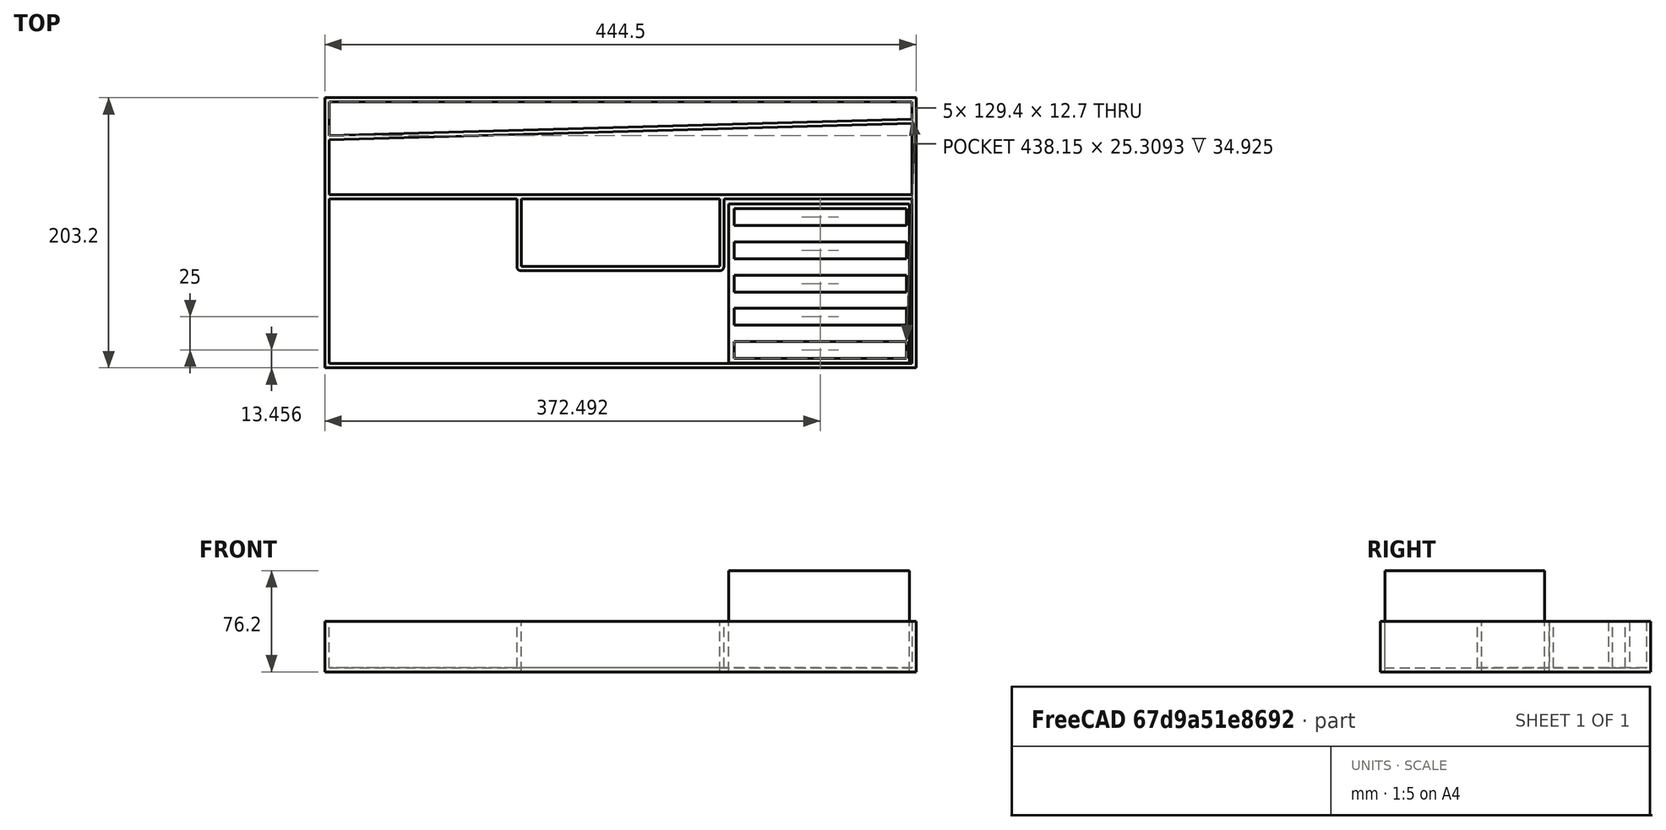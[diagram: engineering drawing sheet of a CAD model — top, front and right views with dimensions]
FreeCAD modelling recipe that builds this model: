
FCSTD DOCUMENT  (FreeCAD 0.19R24291 (Git))
Label: Tray
License: All rights reserved
LicenseURL: http://en.wikipedia.org/wiki/All_rights_reserved
objects: TechDraw::DrawViewDimension×15, Sketcher::SketchObject×5, PartDesign::Pad×4, TechDraw::DrawProjGroupItem×3, PartDesign::Body×2, App::Part×2, TechDraw::DrawSVGTemplate×2, TechDraw::DrawProjGroup×2, TechDraw::DrawPage×2, Spreadsheet::Sheet×1, PartDesign::Thickness×1, PartDesign::Pocket×1, PartDesign::LinearPattern×1
note: 20 computed .brp shape members not serialized (recipe doc carries the construction recipe); baked Part::Feature solids carry a one-line shape summary decoded from their .brp

FEATURE [Sketcher::SketchObject] Sketch
  FullyConstrained = true
  MapMode = 5
  Support = -> [XY_Plane001]
  expr: Constraints[21] = <<SpreadsheetTray>>.HandelPocket_x
  expr: Constraints[20] = <<SpreadsheetTray>>.HandelPocket_y
  expr: Constraints[10] = <<SpreadsheetTray>>.Width_y
  expr: Constraints[9] = <<SpreadsheetTray>>.Length_x
  sketch-geometry (8):
    g0: LineSegment StartX=-222.25 StartY=101.6 StartZ=0 EndX=222.25 EndY=101.6 EndZ=0
    g1: LineSegment StartX=222.25 StartY=101.6 StartZ=0 EndX=222.25 EndY=-101.6 EndZ=0
    g2: LineSegment StartX=222.25 StartY=-101.6 StartZ=0 EndX=-222.25 EndY=-101.6 EndZ=0
    g3: LineSegment StartX=-222.25 StartY=-101.6 StartZ=0 EndX=-222.25 EndY=101.6 EndZ=0
    g4: LineSegment StartX=-74.6125 StartY=25.4 StartZ=0 EndX=74.6125 EndY=25.4 EndZ=0
    g5: LineSegment StartX=74.6125 StartY=25.4 StartZ=0 EndX=74.6125 EndY=-25.4 EndZ=0
    g6: LineSegment StartX=74.6125 StartY=-25.4 StartZ=0 EndX=-74.6125 EndY=-25.4 EndZ=0
    g7: LineSegment StartX=-74.6125 StartY=-25.4 StartZ=0 EndX=-74.6125 EndY=25.4 EndZ=0
  constraints (22):
    c: Coincident(g0,g1)
    c: Coincident(g1,g2)
    c: Coincident(g2,g3)
    c: Coincident(g3,g0)
    c: Horizontal(g0)
    c: Horizontal(g2)
    c: Vertical(g1)
    c: Vertical(g3)
    c: Symmetric(g0,g1,g-1)
    c: DistanceX(g0,g0) = 444.5
    c: DistanceY(g2,g0) = 203.2
    c: Coincident(g4,g5)
    c: Coincident(g5,g6)
    c: Coincident(g6,g7)
    c: Coincident(g7,g4)
    c: Horizontal(g4)
    c: Horizontal(g6)
    c: Vertical(g5)
    c: Vertical(g7)
    c: Symmetric(g4,g5,g-1)
    c: DistanceY(g5,g4) = 50.8
    c: DistanceX(g6,g5) = 149.225
FEATURE [Spreadsheet::Sheet] Spreadsheet  label="SpreadsheetTray"
  cells = A2=Tray; A4=Length_x; B4(Length_x)==17.5in; C4=HalfLength; D4(HalfLength)==B4 / 2; A5=Width_y; B5(Width_y)==8in; C5=HalfWidth; D5(HalfWidth)==B5 / 2; A6=Height_z; B6(Height_z)==1.5in; A8=Thickness; B8(Thickness)==0.125"; A10=HandelPocket_x; B10(HandelPocket_x)==5.875"; A11=HandelPocket_y; B11(HandelPocket_y)==2"
FEATURE [PartDesign::Pad] Pad  label="PadHeight_z"
  Direction = (1,1,1)
  Length = 38.1
  Length2 = 99.9998
  Profile = -> Sketch
  Type = 0
  expr: Length = <<SpreadsheetTray>>.Height_z
FEATURE [PartDesign::Thickness] Thickness
  Base = -> Pad [Face10]
  BaseFeature = -> Pad
  Intersection = false
  Join = 0
  Mode = 0
  Reversed = true
  SupportTransform = false
  Value = 3.175
  expr: Value = <<SpreadsheetTray>>.Thickness
FEATURE [Sketcher::SketchObject] Sketch001
  FullyConstrained = true
  MapMode = 5
  Support = -> [XY_Plane001]
  expr: Constraints[10] = 1"
  expr: Constraints[9] = <<SpreadsheetTray>>.Length_x
  expr: Constraints[8] = <<SpreadsheetTray>>.Thickness
  sketch-geometry (4):
    g0: LineSegment StartX=-222.25 StartY=28.575 StartZ=0 EndX=222.25 EndY=28.575 EndZ=0
    g1: LineSegment StartX=222.25 StartY=28.575 StartZ=0 EndX=222.25 EndY=25.4 EndZ=0
    g2: LineSegment StartX=222.25 StartY=25.4 StartZ=0 EndX=-222.25 EndY=25.4 EndZ=0
    g3: LineSegment StartX=-222.25 StartY=25.4 StartZ=0 EndX=-222.25 EndY=28.575 EndZ=0
  constraints (11):
    c: Coincident(g0,g1)
    c: Coincident(g1,g2)
    c: Coincident(g2,g3)
    c: Coincident(g3,g0)
    c: Horizontal(g2)
    c: Vertical(g1)
    c: Vertical(g3)
    c: Symmetric(g0,g0,g-2)
    c: DistanceY(g2,g0) = 3.175
    c: DistanceX(g2,g1) = 444.5
    c: DistanceY(g-1,g2) = 25.4
FEATURE [PartDesign::Pad] Pad001  label="PadDivider1"
  BaseFeature = -> Thickness
  Direction = (1,1,1)
  Length = 38.1
  Length2 = 99.9998
  Profile = -> Sketch001
  Type = 0
  expr: Length = <<SpreadsheetTray>>.Height_z
FEATURE [Sketcher::SketchObject] Sketch002
  FullyConstrained = true
  MapMode = 5
  Support = -> [XY_Plane001]
  expr: Constraints[11] = <<SpreadsheetTray>>.Length_x / 2
  expr: Constraints[10] = <<SpreadsheetTray>>.Length_x / 2
  expr: Constraints[7] = <<SpreadsheetTray>>.Thickness
  sketch-geometry (4):
    g0: LineSegment StartX=-222.25 StartY=73.025 StartZ=0 EndX=-222.25 EndY=69.85 EndZ=0
    g1: LineSegment StartX=-222.25 StartY=69.85 StartZ=0 EndX=222.25 EndY=82.55 EndZ=0
    g2: LineSegment StartX=222.25 StartY=82.55 StartZ=0 EndX=222.25 EndY=85.725 EndZ=0
    g3: LineSegment StartX=222.25 StartY=85.725 StartZ=0 EndX=-222.25 EndY=73.025 EndZ=0
  constraints (12):
    c: Vertical(g0)
    c: Coincident(g0,g1)
    c: Coincident(g1,g2)
    c: Vertical(g2)
    c: Coincident(g2,g3)
    c: Coincident(g3,g0)
    c: Equal(g0,g2)
    c: DistanceY(g0,g0) = 3.175
    c: DistanceY(g-1,g0) = 69.85
    c: DistanceY(g-1,g1) = 82.55
    c: DistanceX(g0,g-1) = 222.25
    c: DistanceX(g-1,g1) = 222.25
FEATURE [PartDesign::Pad] Pad002  label="PadDivider2"
  BaseFeature = -> Pad001
  Direction = (1,1,1)
  Length = 38.1
  Length2 = 99.9998
  Profile = -> Sketch002
  Type = 0
  expr: Length = <<SpreadsheetTray>>.Height_z
FEATURE [PartDesign::Body] Body  label="BodyTray"
  Group = -> [Sketch,Pad,Thickness,Sketch001,Pad001,Sketch002,Pad002]
  Origin = -> Origin001
  Tip = -> Pad002
FEATURE [App::Part] Part  label="PartTray"
  Group = -> [Body]
  Origin = -> Origin
FEATURE [TechDraw::DrawSVGTemplate] Template
  EditableTexts = Approved1=Approved 1; Approved2=Approved 2; CheckedBy=on 20230717; Code=Code; CompanyAddress=3433 Ridgeway Trail, Maryville TN 37801; CompanyName=Amused Scientist; DrawingNumber=Drawing Number; DrawingTitle1=ToolBoxTray_18x8_5_in; DrawingTitle2=Drawing Title 2; DrawingTitle3=Drawing Title 3; DrawnBy=(Forrest) Lee Erickson; Revision=Rev 1; Scale=Scale; Sheet=Sheet n of m
  Height = 215.9
  Orientation = 1
  Width = 279.4
FEATURE [TechDraw::DrawProjGroupItem] ProjItem  label="Front"
  CoarseView = false
  Direction = (0,0,1)
  Focus = 100
  HardHidden = false
  IsoCount = 0
  IsoHidden = false
  IsoVisible = false
  LockPosition = true
  Perspective = false
  Rotation = 0
  RotationVector = (1,0,0)
  Scale = 0.5
  ScaleType = 2
  SeamHidden = false
  SeamVisible = false
  SmoothHidden = false
  SmoothVisible = false
  Source = -> [Body]
  Type = 0
  X = 0
  XDirection = (1,0,0)
  Y = 0
FEATURE [TechDraw::DrawProjGroup] ProjGroup
  Anchor = -> ProjItem
  AutoDistribute = true
  LockPosition = false
  ProjectionType = 0
  Rotation = 0
  Scale = 0.5
  ScaleType = 2
  Source = -> [Body]
  Views = -> [ProjItem]
  X = 145.502
  Y = 130.742
  spacingX = 15.0114
  spacingY = 15.0114
FEATURE [TechDraw::DrawViewDimension] Dimension
  Arbitrary = false
  ArbitraryTolerances = false
  EqualTolerance = true
  FormatSpec = %.3f
  FormatSpecOverTolerance = %+.3f
  FormatSpecUnderTolerance = %+.3f
  Inverted = false
  LockPosition = false
  MeasureType = 1
  OverTolerance = 0
  References2D = -> [ProjItem]
  Rotation = 0
  ScaleType = 0
  TheoreticalExact = false
  Type = 2
  UnderTolerance = 0
  X = -125.171
  Y = -0.389136
FEATURE [TechDraw::DrawViewDimension] Dimension001
  Arbitrary = false
  ArbitraryTolerances = false
  EqualTolerance = true
  FormatSpec = %.3f
  FormatSpecOverTolerance = %+.3f
  FormatSpecUnderTolerance = %+.3f
  Inverted = false
  LockPosition = false
  MeasureType = 1
  OverTolerance = 0
  References2D = -> [ProjItem]
  Rotation = 0
  ScaleType = 0
  TheoreticalExact = false
  Type = 2
  UnderTolerance = 0
  X = -119.625
  Y = -19.5172
FEATURE [TechDraw::DrawViewDimension] Dimension002
  Arbitrary = false
  ArbitraryTolerances = false
  EqualTolerance = true
  FormatSpec = %.3f
  FormatSpecOverTolerance = %+.3f
  FormatSpecUnderTolerance = %+.3f
  Inverted = false
  LockPosition = false
  MeasureType = 1
  OverTolerance = 0
  References2D = -> [ProjItem]
  Rotation = 0
  ScaleType = 0
  TheoreticalExact = false
  Type = 2
  UnderTolerance = 0
  X = -107.502
  Y = -12.4802
FEATURE [TechDraw::DrawViewDimension] Dimension003
  Arbitrary = false
  ArbitraryTolerances = false
  EqualTolerance = true
  FormatSpec = %.3f
  FormatSpecOverTolerance = %+.3f
  FormatSpecUnderTolerance = %+.3f
  Inverted = false
  LockPosition = false
  MeasureType = 1
  OverTolerance = 0
  References2D = -> [ProjItem]
  Rotation = 0
  ScaleType = 0
  TheoreticalExact = false
  Type = 2
  UnderTolerance = 0
  X = 114.332
  Y = -3.75162
FEATURE [TechDraw::DrawViewDimension] Dimension004
  Arbitrary = false
  ArbitraryTolerances = false
  EqualTolerance = true
  FormatSpec = %.3f
  FormatSpecOverTolerance = %+.3f
  FormatSpecUnderTolerance = %+.3f
  Inverted = false
  LockPosition = false
  MeasureType = 1
  OverTolerance = 0
  References2D = -> [ProjItem]
  Rotation = 0
  ScaleType = 0
  TheoreticalExact = false
  Type = 1
  UnderTolerance = 0
  X = 0.279781
  Y = -59.7642
FEATURE [TechDraw::DrawViewDimension] Dimension009
  Arbitrary = false
  ArbitraryTolerances = false
  EqualTolerance = true
  FormatSpec = %.3f
  FormatSpecOverTolerance = %+.3f
  FormatSpecUnderTolerance = %+.3f
  Inverted = false
  LockPosition = false
  MeasureType = 1
  OverTolerance = 0
  References2D = -> [ProjItem]
  Rotation = 0
  ScaleType = 0
  TheoreticalExact = false
  Type = 1
  UnderTolerance = 0
  X = -73.7993
  Y = -7.08606
FEATURE [TechDraw::DrawViewDimension] Dimension010
  Arbitrary = false
  ArbitraryTolerances = false
  EqualTolerance = true
  FormatSpec = %.3f
  FormatSpecOverTolerance = %+.3f
  FormatSpecUnderTolerance = %+.3f
  Inverted = false
  LockPosition = false
  MeasureType = 1
  OverTolerance = 0
  References2D = -> [ProjItem]
  Rotation = 0
  ScaleType = 0
  TheoreticalExact = false
  Type = 2
  UnderTolerance = 0
  X = -43.7229
  Y = -34.5256
FEATURE [TechDraw::DrawViewDimension] Dimension011
  Arbitrary = false
  ArbitraryTolerances = false
  EqualTolerance = true
  FormatSpec = %.3f
  FormatSpecOverTolerance = %+.3f
  FormatSpecUnderTolerance = %+.3f
  Inverted = false
  LockPosition = false
  MeasureType = 1
  OverTolerance = 0
  References2D = -> [ProjItem]
  Rotation = 0
  ScaleType = 0
  TheoreticalExact = false
  Type = 1
  UnderTolerance = 0
  X = 1.34925
  Y = -1.42411
FEATURE [TechDraw::DrawViewDimension] Dimension012
  Arbitrary = false
  ArbitraryTolerances = false
  EqualTolerance = true
  FormatSpec = %.3f
  FormatSpecOverTolerance = %+.3f
  FormatSpecUnderTolerance = %+.3f
  Inverted = false
  LockPosition = false
  MeasureType = 1
  OverTolerance = 0
  References2D = -> [ProjItem]
  Rotation = 0
  ScaleType = 0
  TheoreticalExact = false
  Type = 2
  UnderTolerance = 0
  X = -115.699
  Y = 67.5759
FEATURE [TechDraw::DrawViewDimension] Dimension013
  Arbitrary = false
  ArbitraryTolerances = false
  EqualTolerance = true
  FormatSpec = %.3f
  FormatSpecOverTolerance = %+.3f
  FormatSpecUnderTolerance = %+.3f
  Inverted = false
  LockPosition = false
  MeasureType = 1
  OverTolerance = 0
  References2D = -> [ProjItem]
  Rotation = 0
  ScaleType = 0
  TheoreticalExact = false
  Type = 2
  UnderTolerance = 0
  X = 103.335
  Y = 64.2579
FEATURE [TechDraw::DrawViewDimension] Dimension014
  Arbitrary = false
  ArbitraryTolerances = false
  EqualTolerance = true
  FormatSpec = %.3f
  FormatSpecOverTolerance = %+.3f
  FormatSpecUnderTolerance = %+.3f
  Inverted = false
  LockPosition = false
  MeasureType = 1
  OverTolerance = 0
  References2D = -> [ProjItem]
  Rotation = 0
  ScaleType = 0
  TheoreticalExact = false
  Type = 2
  UnderTolerance = 0
  X = 103.404
  Y = 27.0414
FEATURE [TechDraw::DrawPage] Page  label="PageTray"
  KeepUpdated = true
  NextBalloonIndex = 1
  ProjectionType = 0
  Template = -> Template
  Views = -> [ProjGroup,Dimension,Dimension001,Dimension002,Dimension003,Dimension004,Dimension009,Dimension010,Dimension011,Dimension012,Dimension013,Dimension014]
FEATURE [Sketcher::SketchObject] Sketch003
  FullyConstrained = false
  MapMode = 5
  Support = -> [XY_Plane003]
  sketch-geometry (4):
    g0: LineSegment StartX=81.3447 StartY=21.8412 StartZ=0 EndX=217.227 EndY=21.8412 EndZ=0
    g1: LineSegment StartX=217.227 StartY=21.8412 StartZ=0 EndX=217.227 EndY=-97.9502 EndZ=0
    g2: LineSegment StartX=217.227 StartY=-97.9502 StartZ=0 EndX=81.3447 EndY=-97.9502 EndZ=0
    g3: LineSegment StartX=81.3447 StartY=-97.9502 StartZ=0 EndX=81.3447 EndY=21.8412 EndZ=0
  constraints (8):
    c: Coincident(g0,g1)
    c: Coincident(g1,g2)
    c: Coincident(g2,g3)
    c: Coincident(g3,g0)
    c: Horizontal(g0)
    c: Horizontal(g2)
    c: Vertical(g1)
    c: Vertical(g3)
FEATURE [PartDesign::Pad] Pad003  label="PadPlierHolder"
  Direction = (1,1,1)
  Length = 76.2
  Length2 = 99.9998
  Profile = -> Sketch003
  Type = 0
  expr: Length = <<SpreadsheetTray>>.Height_z * 2
FEATURE [Sketcher::SketchObject] Sketch004
  FullyConstrained = false
  MapMode = 5
  Placement = pos=(0,0,76.2) rot=(0,0,1;0rad)
  Support = -> [Pad003]
  sketch-geometry (4):
    g0: LineSegment StartX=85.5408 StartY=-81.7944 StartZ=0 EndX=214.944 EndY=-81.7944 EndZ=0
    g1: LineSegment StartX=214.944 StartY=-81.7944 StartZ=0 EndX=214.944 EndY=-94.4944 EndZ=0
    g2: LineSegment StartX=214.944 StartY=-94.4944 StartZ=0 EndX=85.5408 EndY=-94.4944 EndZ=0
    g3: LineSegment StartX=85.5408 StartY=-94.4944 StartZ=0 EndX=85.5408 EndY=-81.7944 EndZ=0
  constraints (9):
    c: Coincident(g0,g1)
    c: Coincident(g1,g2)
    c: Coincident(g2,g3)
    c: Coincident(g3,g0)
    c: Horizontal(g0)
    c: Horizontal(g2)
    c: Vertical(g1)
    c: Vertical(g3)
    c: DistanceY(g2,g0) = 12.7
FEATURE [PartDesign::Pocket] Pocket
  BaseFeature = -> Pad003
  Length = 5.0038
  Length2 = 99.9998
  Profile = -> Sketch004
  Type = 1
FEATURE [PartDesign::LinearPattern] LinearPattern
  BaseFeature = -> Pocket
  Direction = -> Sketch004 [V_Axis]
  Length = 100
  Occurrences = 5
  Originals = -> [Pocket]
FEATURE [PartDesign::Body] Body001  label="BodyPlierHolder"
  Group = -> [Sketch003,Pad003,Sketch004,Pocket,LinearPattern]
  Origin = -> Origin003
  Tip = -> LinearPattern
FEATURE [App::Part] Part001  label="PartPlierHolder"
  Group = -> [Body001]
  Origin = -> Origin002
FEATURE [TechDraw::DrawSVGTemplate] Template001
  EditableTexts = Approved1=Approved 1; Approved2=Approved 2; CheckedBy=on 20230717; Code=Code; CompanyAddress=3433 Ridgeway Trail, Maryville TN 37801; CompanyName=Amused Scientist; DrawingNumber=Drawing Number; DrawingTitle1=Plier Holder; DrawingTitle2=Drawing Title 2; DrawingTitle3=Drawing Title 3; DrawnBy=(Forrest) Lee Erickson; Revision=Rev1; Scale=Scale; Sheet=Sheet 2 of m
  Height = 215.9
  Orientation = 1
  Width = 279.4
FEATURE [TechDraw::DrawProjGroupItem] ProjItem001  label="Front001"
  CoarseView = false
  Direction = (0,0,1)
  Focus = 100
  HardHidden = false
  IsoCount = 0
  IsoHidden = false
  IsoVisible = false
  LockPosition = true
  Perspective = false
  Rotation = 0
  RotationVector = (1,0,0)
  Scale = 0.5
  ScaleType = 2
  SeamHidden = false
  SeamVisible = false
  SmoothHidden = false
  SmoothVisible = false
  Source = -> [Body001]
  Type = 0
  X = 0
  XDirection = (1,0,0)
  Y = 0
FEATURE [TechDraw::DrawProjGroupItem] ProjItem002  label="FrontTopRight"
  CoarseView = false
  Direction = (0.57735,0.57735,0.57735)
  Focus = 100
  HardHidden = false
  IsoCount = 0
  IsoHidden = false
  IsoVisible = false
  LockPosition = true
  Perspective = false
  Rotation = 0
  RotationVector = (1,0,0)
  Scale = 0.5
  ScaleType = 2
  SeamHidden = false
  SeamVisible = false
  SmoothHidden = false
  SmoothVisible = false
  Source = -> [Body001]
  Type = 7
  X = 108.266
  XDirection = (0.707107,0,-0.707107)
  Y = 10.1223
FEATURE [TechDraw::DrawProjGroup] ProjGroup001
  Anchor = -> ProjItem001
  AutoDistribute = true
  LockPosition = false
  ProjectionType = 0
  Rotation = 0
  Scale = 0.5
  ScaleType = 2
  Source = -> [Body001]
  Views = -> [ProjItem001,ProjItem002]
  X = 80.0853
  Y = 129.445
  spacingX = 15.0114
  spacingY = 15.0114
FEATURE [TechDraw::DrawViewDimension] Dimension015
  Arbitrary = false
  ArbitraryTolerances = false
  EqualTolerance = true
  FormatSpec = %.3f
  FormatSpecOverTolerance = %+.3f
  FormatSpecUnderTolerance = %+.3f
  Inverted = false
  LockPosition = false
  MeasureType = 1
  OverTolerance = 0
  References2D = -> [ProjItem001]
  Rotation = 0
  ScaleType = 0
  TheoreticalExact = false
  Type = 2
  UnderTolerance = 0
  X = -43.5786
  Y = -24.5889
FEATURE [TechDraw::DrawViewDimension] Dimension016
  Arbitrary = false
  ArbitraryTolerances = false
  EqualTolerance = true
  FormatSpec = %.3f
  FormatSpecOverTolerance = %+.3f
  FormatSpecUnderTolerance = %+.3f
  Inverted = false
  LockPosition = false
  MeasureType = 1
  OverTolerance = 0
  References2D = -> [ProjItem001]
  Rotation = 0
  ScaleType = 0
  TheoreticalExact = false
  Type = 2
  UnderTolerance = 0
  X = 36.1256
  Y = -1.19481
FEATURE [TechDraw::DrawViewDimension] Dimension017
  Arbitrary = false
  ArbitraryTolerances = false
  EqualTolerance = true
  FormatSpec = %.3f
  FormatSpecOverTolerance = %+.3f
  FormatSpecUnderTolerance = %+.3f
  Inverted = false
  LockPosition = false
  MeasureType = 1
  OverTolerance = 0
  References2D = -> [ProjItem001]
  Rotation = 0
  ScaleType = 0
  TheoreticalExact = false
  Type = 1
  UnderTolerance = 0
  X = -0.738096
  Y = -36.8854
FEATURE [TechDraw::DrawViewDimension] Dimension018
  Arbitrary = false
  ArbitraryTolerances = false
  EqualTolerance = true
  FormatSpec = %.3f
  FormatSpecOverTolerance = %+.3f
  FormatSpecUnderTolerance = %+.3f
  Inverted = false
  LockPosition = false
  MeasureType = 1
  OverTolerance = 0
  References2D = -> [ProjItem001]
  Rotation = 0
  ScaleType = 0
  TheoreticalExact = false
  Type = 2
  UnderTolerance = 0
  X = 49.3586
  Y = -1.99843
FEATURE [TechDraw::DrawPage] Page001  label="PagePlierHolder"
  KeepUpdated = true
  NextBalloonIndex = 1
  ProjectionType = 0
  Template = -> Template001
  Views = -> [ProjGroup001,Dimension015,Dimension016,Dimension017,Dimension018]
